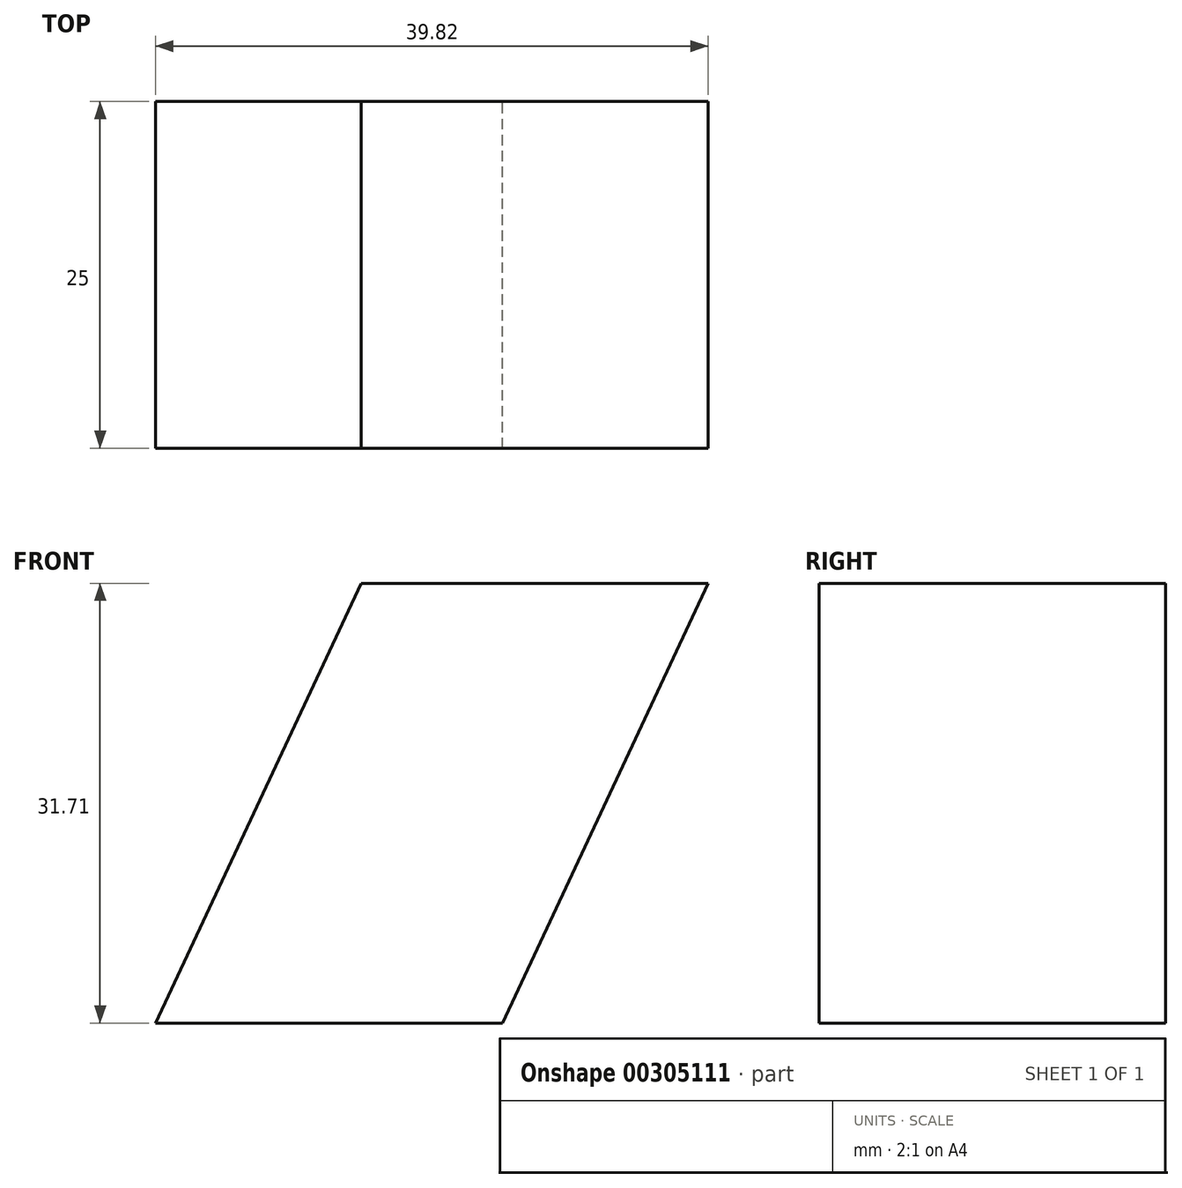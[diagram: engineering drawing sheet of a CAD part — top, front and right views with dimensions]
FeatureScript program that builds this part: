
annotation { "Feature Type Name" : "Feature", "Feature Type Description" : "" }
export const myFeature = defineFeature(function(context is Context, id is Id, definition is map)
    precondition{}
    {
        {
            var Q0;
            Q0=qCreatedBy(makeId("Front.planeOp"),FACE);
            var sketch = newSketch(context, id + "F0", { "sketchPlane" : qUnion([Q0])});
            skLineSegment(sketch, "E0", {"start": v(-37.3, -38.06) * mm, "end": v(-22.48, -6.35) * mm});
            skLineSegment(sketch, "E1", {"start": v(-22.48, -6.35) * mm, "end": v(2.52, -6.35) * mm});
            skLineSegment(sketch, "E2", {"start": v(-37.3, -38.06) * mm, "end": v(-12.3, -38.06) * mm});
            skLineSegment(sketch, "E3", {"start": v(-12.3, -38.06) * mm, "end": v(2.52, -6.35) * mm});
            skSolve(sketch);
        }
        {
            var Q0;
            Q0=makeQuery(id+"F0.imprint","IMPRINT",FACE,{"disambiguationData":[TD([[makeQuery(id+"F0.imprint","IMPRINT",EDGE,{"derivedFrom":sQuery(id+"F0.wireOp",EDGE,"E0")}),-1.0]])]});
            extrude(context, id + "F1", {"entities" : qUnion([Q0]), "depth" : 25 * mm});
        }
    });
